# Revit family: Differenzdruckregler 4202 FIX 23kPa
name_source: partatom
category: Rohrzubehör
units: mm (PartAtom-declared; Revit-internal decimal feet)

## family parameters
Arbeitsebenenbasiert = Nein
Beim Laden mit Abzugskörper schneiden = Nein
Bemaßung runder Anschluss = Durchmesser verwenden
Gemeinsam genutzt = Nein
Immer vertikal = Ja
OmniClass-Nummer = 23.65.55.14
OmniClass-Titel = Valves for Liquid Services
Teiletyp = Unterbricht

## types (2) — shared parameters
Anschlussnippel = Messing CW602N
Anwendungsgebiet = Der Differenzdruckregler ist ein Regler mit linearer Kennlinie in Geradsitzausführung und arbeitet ohne Hilfsenergie. Der Differenzdruck-Sollwert beträgt 23 kPa, 50 kPa bzw 13 kPa. Im Lieferumfang enthalten ist die Impulsleitung (1000 mm), diese ist mit einem Strangregulierventil im Vorlauf zu verbinden.
B01 = 10 mm  [stored 0.0328084 ft]
B02 = 104.688 mm
B03 = 44.5 mm  [stored 0.145997 ft]
B04 = 100.649 mm
Druckfeder = Federstahl, rost-und säurebeständig
Dämmschale = EPP (expandiertes Polypropylen)
Gehäuse = DZR Messing CC770S
H03 = 9.8 mm
H04 = 4 mm  [stored 0.0131234 ft]
Hersteller = HERZ-Armaturen Ges.m.b.H
Hinweise zum Material = Gemäß Art 33 der REACH-Verordnung (EG Nr. 1907/2006) sind wir verpflichtet, darauf hinzuweisen,
dass der Stoff Blei auf der SVHC-Liste geführt wird und dass alle aus Messing bestehenden Bauteile,
die in unseren Erzeugnissen verarbeitet sind, mehr als 0,1 % (w/w) Blei (CAS: 7439-92-1 / EINECS:
231-100-4) enthalten. Da Blei als Legierungsbestandteil fest gebunden ist, sind keine Expositionen zu
erwarten und daher sind keine zusätzlichen Angaben zur sicheren Verwendung notwendig.

Im Hanf enthaltenes Ammoniak schädigt
Messingventilgehäuse, EPDM Dichtungen werden durch
Mineralöle bzw. mineralölhaltige Schmierstoffe aufgequollen
und führen somit zum Ausfall der EPDM-Dichtungen. Für
Frost- und Korrosionsschutzmittel auf der Basis von Ethylen- und Propylenglykol sind die entsprechenden
Angaben den Unterlagen des Herstellers zu entnehmen.
J1 = 6.5 mm
J10 = 18.897 mm  [stored 0.061998 ft]
J11 = 3.5 mm  [stored 0.0114829 ft]
J2 = 11 mm
J3 = 3.2 mm
J4 = 1.5 mm  [stored 0.00492126 ft]
J5 = 6.5 mm
J6 = 3.9 mm
J7 = 15.897 mm
J8 = 7.85 mm
J9 = 15.7 mm
K1 = 7.651 mm
K1.1 = 2.35 mm
K10 = 18.25 mm
K11 = 35 mm  [stored 0.114829 ft]
K12 = 10 mm  [stored 0.0328084 ft]
K13 = 16.649 mm  [stored 0.0546227 ft]
K14 = 16.649 mm  [stored 0.0546227 ft]
K15 = 26.649 mm
K16 = 3 mm  [stored 0.00984252 ft]
K17 = 66.7 mm
K18 = 89 mm  [stored 0.291995 ft]
K2 = 2.35 mm
K3 = 15 mm
K4 = 12 mm  [stored 0.0393701 ft]
K5 = 13 mm
K6 = 11.7 mm
K7 = 8.7 mm
K8 = 55 mm
K9 = 4 mm  [stored 0.0131234 ft]
Max. Betriebsdruck = 2500000.0 Pa
Max. Differenzdruck am Gehäuse = 400000.0 Pa
Max. zulässige Betriebstemperatur DN40 - DN50 = 110 °C
Max. zulässige Betriebstemperatur bis DN32 = 130 °C
Medium = Wasserbeschaffenheit nach ÖNORM H 5195 und VDI 2035
Die Verwendung von Ethylen- und Propylenglykol ist im
Mischungsverhältnis 25 - 50 Vol.-% zulässig.
Membrane = EPDM
Membrangehäuse = Messing CW602N
Min. Betriebstemperatur (Frostschutz) = -20 °C
Min. Betriebstemperatur (reines Wasser) = 2 °C
O-Ringe = EPDM
R02 = 14.5 mm  [stored 0.0475722 ft]
Regelbereich = FIX 23kPa
Regleranschlussmutter = Messing CW614N
SCRNCODE = 05;03;4
SCRNSEQ = ARM;ARM_TYP="DIFR";2
URL = www.herz-armaturen.at
Ventilschaft = Edelstahl 14301
zero-valued in all types: Vorgabe-Ansicht

## per-type parameters (varying)
| type | Dämmung |
| Mit Dämmung | Ja |
| Ohne Dämmung | Nein |

note: [stored X ft] marks values corroborated as IEEE doubles in the binary element streams (Revit-internal decimal feet)
